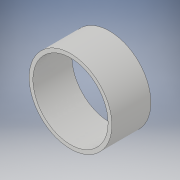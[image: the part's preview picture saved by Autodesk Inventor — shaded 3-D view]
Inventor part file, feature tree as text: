
AUTODESK INVENTOR PART (.ipt)
format: ipt  version: 2019 (Build 230136000, 136)  size: 102,912 bytes
history: native  units: mm
features: extrude x2, sketch x2
ambient origin geometry x8: Origin, YZ Plane, XZ Plane, XY Plane, X Axis, Y Axis, Z Axis, Center Point
bodies: Solid1 (feature_tree)
feature tree (4):
  extrude  "Extrusion1"  Depth=4.44mm TaperAngle=0.0deg
  extrude  "Extrusion2"  Depth=4.44mm TaperAngle=0.0deg
  sketch  "Sketch1"  dims[d0=9.42mm d1=4.44mm d2=0.0mm]
  sketch  "Sketch2"  dims[d3=8.56mm d4=4.44mm d5=0.0mm]
